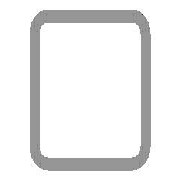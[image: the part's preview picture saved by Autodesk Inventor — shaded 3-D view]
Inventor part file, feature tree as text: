
AUTODESK INVENTOR PART (.ipt)
format: ipt  version: 2025.3 (Build 293356000, 356)  size: 134,656 bytes
history: native  units: mm (DEFAULTED — no unit token found)
features: other x4, sketch x1, plane x1
ambient origin geometry x8: Origin, YZ Plane, XZ Plane, XY Plane, X Axis, Y Axis, Z Axis, Center Point
bodies: Solid1 (feature_tree), Body (feature_tree)
feature tree (6):
  parser-record x1  (decoder bookkeeping rows leaked as tree rows — omitted from the tree; the rows remain in map.json)
  other  "Driven Length"
  other  "Start Plane"
  other  "End Plane"
  sketch  "Sketch3"  dims[d3=2040.0mm d4=0.0mm d7=6.0mm d9=80.0mm d11=80.0mm d12=3.0mm d13=80.0mm d14=2120.0mm d15=40.0mm d16=40.0mm d17=90.0deg d18=2040.0mm]
  plane  "Work Plane3"
